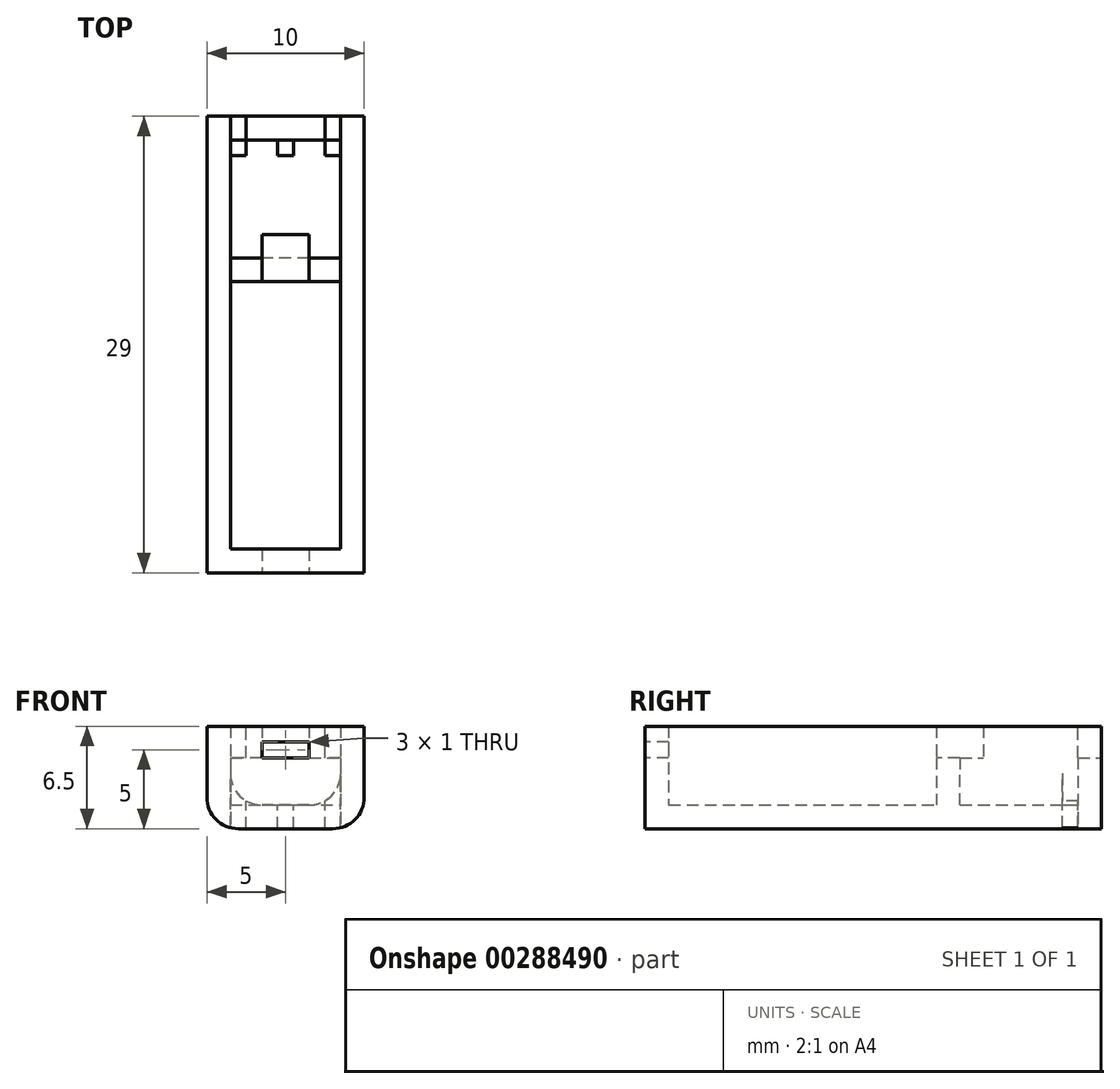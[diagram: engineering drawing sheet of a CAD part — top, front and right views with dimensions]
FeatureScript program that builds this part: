
annotation { "Feature Type Name" : "Feature", "Feature Type Description" : "" }
export const myFeature = defineFeature(function(context is Context, id is Id, definition is map)
    precondition{}
    {
        {
            var Q0;
            Q0=qCreatedBy(makeId("Top.planeOp"),FACE);
            var sketch = newSketch(context, id + "F0", { "sketchPlane" : qUnion([Q0])});
            skLineSegment(sketch, "E0.bottom", {"start": v(0, 0) * mm, "end": v(7, 0) * mm});
            skLineSegment(sketch, "E0.top", {"start": v(0, 26) * mm, "end": v(7, 26) * mm});
            skLineSegment(sketch, "E0.left", {"start": v(0, 0) * mm, "end": v(0, 26) * mm});
            skLineSegment(sketch, "E0.right", {"start": v(7, 0) * mm, "end": v(7, 26) * mm});
            skLineSegment(sketch, "E1", {"start": v(0, 17) * mm, "end": v(7, 17) * mm});
            skLineSegment(sketch, "E2", {"start": v(7, 17) * mm, "end": v(7, 18.5) * mm});
            skLineSegment(sketch, "E3", {"start": v(7, 18.5) * mm, "end": v(0, 18.5) * mm});
            skLineSegment(sketch, "E4.0", {"start": v(0, 27.5) * mm, "end": v(7, 27.5) * mm});
            skLineSegment(sketch, "E5.0", {"start": v(8.5, 0) * mm, "end": v(8.5, 26) * mm});
            skLineSegment(sketch, "E6.0", {"start": v(0, -1.5) * mm, "end": v(7, -1.5) * mm});
            skLineSegment(sketch, "E7.0", {"start": v(-1.5, 0) * mm, "end": v(-1.5, 26) * mm});
            skLineSegment(sketch, "E8", {"start": v(7, 27.5) * mm, "end": v(8.5, 27.5) * mm});
            skLineSegment(sketch, "E9", {"start": v(8.5, 27.5) * mm, "end": v(8.5, 26) * mm});
            skLineSegment(sketch, "E10", {"start": v(0, 27.5) * mm, "end": v(-1.5, 27.5) * mm});
            skLineSegment(sketch, "E11", {"start": v(-1.5, 27.5) * mm, "end": v(-1.5, 26) * mm});
            skLineSegment(sketch, "E12", {"start": v(7, -1.5) * mm, "end": v(8.5, -1.5) * mm});
            skLineSegment(sketch, "E13", {"start": v(8.5, -1.5) * mm, "end": v(8.5, 0) * mm});
            skLineSegment(sketch, "E14", {"start": v(0, -1.5) * mm, "end": v(-1.5, -1.5) * mm});
            skLineSegment(sketch, "E15", {"start": v(-1.5, -1.5) * mm, "end": v(-1.5, 0) * mm});
            skSolve(sketch);
        }
        {
            var Q0;
            {var subQ4=sQuery(id+"F0.wireOp",EDGE,"E0.bottom");Q0=makeQuery(id+"F0.imprint","IMPRINT",FACE,{"disambiguationData":[TD([[makeQuery(id+"F0.imprint","IMPRINT",EDGE,{"derivedFrom":subQ4}),-1.0]])]});}
            var Q1;
            {var subQ0=sQuery(id+"F0.wireOp",EDGE,"E1");Q1=makeQuery(id+"F0.imprint","IMPRINT",FACE,{"disambiguationData":[TD([[makeQuery(id+"F0.imprint","IMPRINT",EDGE,{"derivedFrom":subQ0}),1.0]])]});}
            extrude(context, id + "F1", {"entities" : qUnion([Q0, Q1]), "depth" : 3 * mm});
        }
        {
            var Q0;
            Q0=makeQuery(id+"F1.opExtrude","CAP_FACE",FACE,{"disambiguationData":[OSD([sQuery(id+"F0.wireOp",EDGE,"E0.bottom"),sQuery(id+"F0.wireOp",EDGE,"E0.top"),sQuery(id+"F0.wireOp",EDGE,"E0.left"),sQuery(id+"F0.wireOp",EDGE,"E0.right"),sQuery(id+"F0.wireOp",EDGE,"E1"),sQuery(id+"F0.wireOp",EDGE,"E3"),sQuery(id+"F0.wireOp",EDGE,"E4.0"),sQuery(id+"F0.wireOp",EDGE,"E5.0"),sQuery(id+"F0.wireOp",EDGE,"E6.0"),sQuery(id+"F0.wireOp",EDGE,"E7.0"),sQuery(id+"F0.wireOp",EDGE,"E8"),sQuery(id+"F0.wireOp",EDGE,"E9"),sQuery(id+"F0.wireOp",EDGE,"E10"),sQuery(id+"F0.wireOp",EDGE,"E11"),sQuery(id+"F0.wireOp",EDGE,"E12"),sQuery(id+"F0.wireOp",EDGE,"E13"),sQuery(id+"F0.wireOp",EDGE,"E14"),sQuery(id+"F0.wireOp",EDGE,"E15")])],"isStart":false});
            var sketch = newSketch(context, id + "F2", { "sketchPlane" : qUnion([Q0])});
            skLineSegment(sketch, "E16", {"start": v(0, 18.5) * mm, "end": v(0, 17) * mm});
            skLineSegment(sketch, "E17", {"start": v(7, 18.5) * mm, "end": v(7, 17) * mm});
            skSolve(sketch);
        }
        {
            var Q0;
            Q0=makeQuery(id+"F2.imprint","IMPRINT",FACE,{"disambiguationData":[TD([[makeQuery(id+"F2.imprint","IMPRINT",EDGE,{"derivedFrom":sQuery(id+"F2.wireOp",EDGE,"E16")}),-1.0]])]});
            extrude(context, id + "F3", {"entities" : qUnion([Q0]), "operationType" : NewBodyOperationType.ADD, "depth" : 2 * mm});
        }
        {
            var Q0;
            Q0=qCreatedBy(makeId("Top.planeOp"),FACE);
            var sketch = newSketch(context, id + "F4", { "sketchPlane" : qUnion([Q0])});
            skPoint(sketch, "E18.0", {"position": v(-1.5, -1.5) * mm});
            skPoint(sketch, "E19.0", {"position": v(8.5, 27.5) * mm});
            skLineSegment(sketch, "E20.bottom", {"start": v(-1.5, -1.5) * mm, "end": v(8.5, -1.5) * mm});
            skLineSegment(sketch, "E20.top", {"start": v(-1.5, 27.5) * mm, "end": v(8.5, 27.5) * mm});
            skLineSegment(sketch, "E20.left", {"start": v(-1.5, -1.5) * mm, "end": v(-1.5, 27.5) * mm});
            skLineSegment(sketch, "E20.right", {"start": v(8.5, -1.5) * mm, "end": v(8.5, 27.5) * mm});
            skSolve(sketch);
        }
        {
            var Q0;
            Q0=makeQuery(id+"F4.imprint","IMPRINT",FACE,{"disambiguationData":[TD([[makeQuery(id+"F4.imprint","IMPRINT",EDGE,{"derivedFrom":sQuery(id+"F4.wireOp",EDGE,"E20.bottom")}),1.0]])]});
            extrude(context, id + "F5", {"entities" : qUnion([Q0]), "operationType" : NewBodyOperationType.ADD, "oppositeDirection" : true, "depth" : 1.5 * mm});
        }
        {
            var Q0;
            Q0=makeQuery(id+"F1.opExtrude","CAP_FACE",FACE,{"disambiguationData":[OSD([sQuery(id+"F0.wireOp",EDGE,"E0.bottom"),sQuery(id+"F0.wireOp",EDGE,"E0.top"),sQuery(id+"F0.wireOp",EDGE,"E0.left"),sQuery(id+"F0.wireOp",EDGE,"E0.right"),sQuery(id+"F0.wireOp",EDGE,"E1"),sQuery(id+"F0.wireOp",EDGE,"E3"),sQuery(id+"F0.wireOp",EDGE,"E4.0"),sQuery(id+"F0.wireOp",EDGE,"E5.0"),sQuery(id+"F0.wireOp",EDGE,"E6.0"),sQuery(id+"F0.wireOp",EDGE,"E7.0"),sQuery(id+"F0.wireOp",EDGE,"E8"),sQuery(id+"F0.wireOp",EDGE,"E9"),sQuery(id+"F0.wireOp",EDGE,"E10"),sQuery(id+"F0.wireOp",EDGE,"E11"),sQuery(id+"F0.wireOp",EDGE,"E12"),sQuery(id+"F0.wireOp",EDGE,"E13"),sQuery(id+"F0.wireOp",EDGE,"E14"),sQuery(id+"F0.wireOp",EDGE,"E15")])],"isStart":false});
            var sketch = newSketch(context, id + "F6", { "sketchPlane" : qUnion([Q0])});
            skLineSegment(sketch, "E21", {"start": v(3.5, 17) * mm, "end": v(5, 17) * mm});
            skLineSegment(sketch, "E22", {"start": v(5, 17) * mm, "end": v(5, 20) * mm});
            skLineSegment(sketch, "E23", {"start": v(5, 20) * mm, "end": v(2, 20) * mm});
            skLineSegment(sketch, "E24", {"start": v(2, 20) * mm, "end": v(2, 17) * mm});
            skLineSegment(sketch, "E25", {"start": v(2, 17) * mm, "end": v(3.5, 17) * mm});
            skSolve(sketch);
        }
        {
            var Q0;
            {var subQ0=sQuery(id+"F6.wireOp",EDGE,"E23");Q0=makeQuery(id+"F6.imprint","IMPRINT",FACE,{"disambiguationData":[TD([[makeQuery(id+"F6.imprint","IMPRINT",EDGE,{"derivedFrom":subQ0}),1.0]])]});}
            var Q1;
            {var subQ2=sQuery(id+"F6.wireOp",EDGE,"E21");Q1=makeQuery(id+"F6.imprint","IMPRINT",FACE,{"disambiguationData":[TD([[makeQuery(id+"F6.imprint","IMPRINT",EDGE,{"derivedFrom":subQ2}),1.0]])]});}
            extrude(context, id + "F7", {"entities" : qUnion([Q0, Q1]), "operationType" : NewBodyOperationType.ADD, "depth" : 2 * mm});
        }
        {
            var Q0;
            {var subQ4=sQuery(id+"F0.wireOp",EDGE,"E0.top");Q0=makeQuery(id+"F5.boolean.opBoolean","SPLIT",FACE,{"disambiguationData":[TD([makeQuery(id+"F1.opExtrude","SWEPT_FACE",FACE,{"disambiguationData":[OSD([subQ4])]})])],"derivedFrom":makeQuery(id+"F5.opExtrude","CAP_FACE",FACE,{"disambiguationData":[OSD([sQuery(id+"F4.wireOp",EDGE,"E20.bottom"),sQuery(id+"F4.wireOp",EDGE,"E20.top"),sQuery(id+"F4.wireOp",EDGE,"E20.left"),sQuery(id+"F4.wireOp",EDGE,"E20.right")])],"isStart":true})});}
            var sketch = newSketch(context, id + "F8", { "sketchPlane" : qUnion([Q0])});
            skLineSegment(sketch, "E26.bottom", {"start": v(7, 26) * mm, "end": v(6, 26) * mm});
            skLineSegment(sketch, "E26.top", {"start": v(7, 25) * mm, "end": v(6, 25) * mm});
            skLineSegment(sketch, "E26.left", {"start": v(7, 26) * mm, "end": v(7, 25) * mm});
            skLineSegment(sketch, "E26.right", {"start": v(6, 26) * mm, "end": v(6, 25) * mm});
            skLineSegment(sketch, "E27.bottom", {"start": v(0, 26) * mm, "end": v(1, 26) * mm});
            skLineSegment(sketch, "E27.top", {"start": v(0, 25) * mm, "end": v(1, 25) * mm});
            skLineSegment(sketch, "E27.left", {"start": v(0, 26) * mm, "end": v(0, 25) * mm});
            skLineSegment(sketch, "E27.right", {"start": v(1, 26) * mm, "end": v(1, 25) * mm});
            skLineSegment(sketch, "E28", {"start": v(3.5, 26) * mm, "end": v(3, 26) * mm});
            skLineSegment(sketch, "E29", {"start": v(3, 26) * mm, "end": v(3, 25) * mm});
            skLineSegment(sketch, "E30", {"start": v(3, 25) * mm, "end": v(4, 25) * mm});
            skLineSegment(sketch, "E31", {"start": v(4, 25) * mm, "end": v(4, 26) * mm});
            skLineSegment(sketch, "E32", {"start": v(4, 26) * mm, "end": v(3.5, 26) * mm});
            skSolve(sketch);
        }
        {
            var Q0;
            Q0=makeQuery(id+"F8.imprint","IMPRINT",FACE,{"disambiguationData":[TD([[makeQuery(id+"F8.imprint","IMPRINT",EDGE,{"derivedFrom":sQuery(id+"F8.wireOp",EDGE,"E27.bottom")}),-1.0]])]});
            var Q1;
            Q1=makeQuery(id+"F8.imprint","IMPRINT",FACE,{"disambiguationData":[TD([[makeQuery(id+"F8.imprint","IMPRINT",EDGE,{"derivedFrom":sQuery(id+"F8.wireOp",EDGE,"E28")}),-1.0]])]});
            var Q2;
            Q2=makeQuery(id+"F8.imprint","IMPRINT",FACE,{"disambiguationData":[TD([[makeQuery(id+"F8.imprint","IMPRINT",EDGE,{"derivedFrom":sQuery(id+"F8.wireOp",EDGE,"E26.bottom")}),-1.0]])]});
            extrude(context, id + "F9", {"entities" : qUnion([Q0, Q1, Q2]), "operationType" : NewBodyOperationType.REMOVE, "oppositeDirection" : true, "depth" : 25 * mm});
        }
        {
            var Q0;
            {var subQ0=sQuery(id+"F0.wireOp",EDGE,"E14");var subQ1=sQuery(id+"F0.wireOp",EDGE,"E12");var subQ2=sQuery(id+"F0.wireOp",EDGE,"E6.0");Q0=makeQuery(id+"F5.boolean.opBoolean","MERGE",FACE,{"derivedFrom":[makeQuery(id+"F3.boolean.opBoolean","MERGE",FACE,{"derivedFrom":[makeQuery(id+"F1.opExtrude","SWEPT_FACE",FACE,{"disambiguationData":[OSD([subQ2,subQ1,subQ0])]}),makeQuery(id+"F3.opExtrude","SWEPT_FACE",FACE,{"disambiguationData":[OSD([subQ2,subQ1,subQ0])]})]}),makeQuery(id+"F5.opExtrude","SWEPT_FACE",FACE,{"disambiguationData":[OSD([sQuery(id+"F4.wireOp",EDGE,"E20.bottom")])]})]});}
            var sketch = newSketch(context, id + "F10", { "sketchPlane" : qUnion([Q0])});
            skLineSegment(sketch, "E33", {"start": v(3.5, 5) * mm, "end": v(3.5, 4) * mm});
            skPoint(sketch, "E33.endSnap0", {"position": v(3.5, 5) * mm});
            skLineSegment(sketch, "E34", {"start": v(3.5, 4) * mm, "end": v(2, 4) * mm});
            skLineSegment(sketch, "E35", {"start": v(2, 4) * mm, "end": v(2, 3) * mm});
            skLineSegment(sketch, "E36", {"start": v(2, 3) * mm, "end": v(5, 3) * mm});
            skLineSegment(sketch, "E37", {"start": v(5, 3) * mm, "end": v(5, 4) * mm});
            skLineSegment(sketch, "E38", {"start": v(5, 4) * mm, "end": v(3.5, 4) * mm});
            skSolve(sketch);
        }
        {
            var Q0;
            Q0=makeQuery(id+"F10.imprint","IMPRINT",FACE,{"disambiguationData":[TD([[makeQuery(id+"F10.imprint","IMPRINT",EDGE,{"derivedFrom":sQuery(id+"F10.wireOp",EDGE,"E34")}),1.0]])]});
            extrude(context, id + "F11", {"entities" : qUnion([Q0]), "operationType" : NewBodyOperationType.REMOVE, "oppositeDirection" : true, "depth" : 1.5 * mm});
        }
        {
            var Q0;
            Q0=makeQuery(id+"F5.opExtrude","CAP_EDGE",EDGE,{"disambiguationData":[OSD([sQuery(id+"F4.wireOp",EDGE,"E20.left")])],"isStart":false});
            var Q1;
            Q1=makeQuery(id+"F5.opExtrude","CAP_EDGE",EDGE,{"disambiguationData":[OSD([sQuery(id+"F4.wireOp",EDGE,"E20.right")])],"isStart":false});
            var Q2;
            {var subQ0=sQuery(id+"F0.wireOp",EDGE,"E0.left");Q2=makeQuery(id+"F1.opExtrude","CAP_EDGE",EDGE,{"disambiguationData":[OSD([subQ0]),TDD([makeQuery(id+"F0.imprint","IMPRINT",EDGE,{"disambiguationData":[TD([[makeQuery(id+"F0.imprint","INTERSECT",VERTEX,{"derivedFrom":[sQuery(id+"F0.wireOp",EDGE,"E0.bottom"),subQ0]}),-1.0]])],"derivedFrom":subQ0})])],"isStart":true});}
            var Q3;
            {var subQ0=sQuery(id+"F0.wireOp",EDGE,"E0.left");Q3=makeQuery(id+"F1.opExtrude","CAP_EDGE",EDGE,{"disambiguationData":[OSD([subQ0]),TDD([makeQuery(id+"F0.imprint","IMPRINT",EDGE,{"disambiguationData":[TD([[makeQuery(id+"F0.imprint","INTERSECT",VERTEX,{"derivedFrom":[sQuery(id+"F0.wireOp",EDGE,"E0.top"),subQ0]}),1.0]])],"derivedFrom":subQ0})])],"isStart":true});}
            var Q4;
            {var subQ0=sQuery(id+"F0.wireOp",EDGE,"E0.right");Q4=makeQuery(id+"F1.opExtrude","CAP_EDGE",EDGE,{"disambiguationData":[OSD([subQ0]),TDD([makeQuery(id+"F0.imprint","IMPRINT",EDGE,{"disambiguationData":[TD([[makeQuery(id+"F0.imprint","INTERSECT",VERTEX,{"derivedFrom":[sQuery(id+"F0.wireOp",EDGE,"E0.bottom"),subQ0]}),-1.0]])],"derivedFrom":subQ0})])],"isStart":true});}
            var Q5;
            {var subQ0=sQuery(id+"F0.wireOp",EDGE,"E0.right");Q5=makeQuery(id+"F1.opExtrude","CAP_EDGE",EDGE,{"disambiguationData":[OSD([subQ0]),TDD([makeQuery(id+"F0.imprint","IMPRINT",EDGE,{"disambiguationData":[TD([[makeQuery(id+"F0.imprint","INTERSECT",VERTEX,{"derivedFrom":[sQuery(id+"F0.wireOp",EDGE,"E0.top"),subQ0]}),1.0]])],"derivedFrom":subQ0})])],"isStart":true});}
            fillet(context, id + "F12", {"entities" : qUnion([Q0, Q1, Q2, Q3, Q4, Q5]), "radius" : 2 * mm, "tangentPropagation" : true, "allowEdgeOverflow" : false});
        }
        {
            var Q0;
            {var subQ0=sQuery(id+"F0.wireOp",EDGE,"E10");var subQ1=sQuery(id+"F0.wireOp",EDGE,"E8");var subQ2=sQuery(id+"F0.wireOp",EDGE,"E4.0");Q0=makeQuery(id+"F5.boolean.opBoolean","MERGE",FACE,{"derivedFrom":[makeQuery(id+"F3.boolean.opBoolean","MERGE",FACE,{"derivedFrom":[makeQuery(id+"F1.opExtrude","SWEPT_FACE",FACE,{"disambiguationData":[OSD([subQ2,subQ1,subQ0])]}),makeQuery(id+"F3.opExtrude","SWEPT_FACE",FACE,{"disambiguationData":[OSD([subQ2,subQ1,subQ0])]})]}),makeQuery(id+"F5.opExtrude","SWEPT_FACE",FACE,{"disambiguationData":[OSD([sQuery(id+"F4.wireOp",EDGE,"E20.top")])]})]});}
            var sketch = newSketch(context, id + "F13", { "sketchPlane" : qUnion([Q0])});
            skLineSegment(sketch, "E39", {"start": v(-8.5, 5) * mm, "end": v(-7, 5) * mm});
            skLineSegment(sketch, "E40", {"start": v(-7, 5) * mm, "end": v(-7, 3) * mm});
            skLineSegment(sketch, "E41", {"start": v(-7, 3) * mm, "end": v(-6, 3) * mm});
            skLineSegment(sketch, "E42", {"start": v(-6, 3) * mm, "end": v(-6, 5) * mm});
            skLineSegment(sketch, "E43", {"start": v(-6, 5) * mm, "end": v(-7, 5) * mm});
            skLineSegment(sketch, "E44", {"start": v(1.5, 5) * mm, "end": v(0, 5) * mm});
            skLineSegment(sketch, "E45", {"start": v(0, 5) * mm, "end": v(0, 3) * mm});
            skLineSegment(sketch, "E46", {"start": v(0, 3) * mm, "end": v(-1, 3) * mm});
            skLineSegment(sketch, "E47", {"start": v(-1, 3) * mm, "end": v(-1, 5) * mm});
            skLineSegment(sketch, "E48", {"start": v(-1, 5) * mm, "end": v(0, 5) * mm});
            skSolve(sketch);
        }
        {
            var Q0;
            Q0=makeQuery(id+"F13.imprint","IMPRINT",FACE,{"disambiguationData":[TD([[makeQuery(id+"F13.imprint","IMPRINT",EDGE,{"derivedFrom":sQuery(id+"F13.wireOp",EDGE,"E40")}),1.0]])]});
            var Q1;
            Q1=makeQuery(id+"F13.imprint","IMPRINT",FACE,{"disambiguationData":[TD([[makeQuery(id+"F13.imprint","IMPRINT",EDGE,{"derivedFrom":sQuery(id+"F13.wireOp",EDGE,"E45")}),-1.0]])]});
            extrude(context, id + "F14", {"entities" : qUnion([Q0, Q1]), "operationType" : NewBodyOperationType.REMOVE, "oppositeDirection" : true, "depth" : 1.5 * mm});
        }
    });
